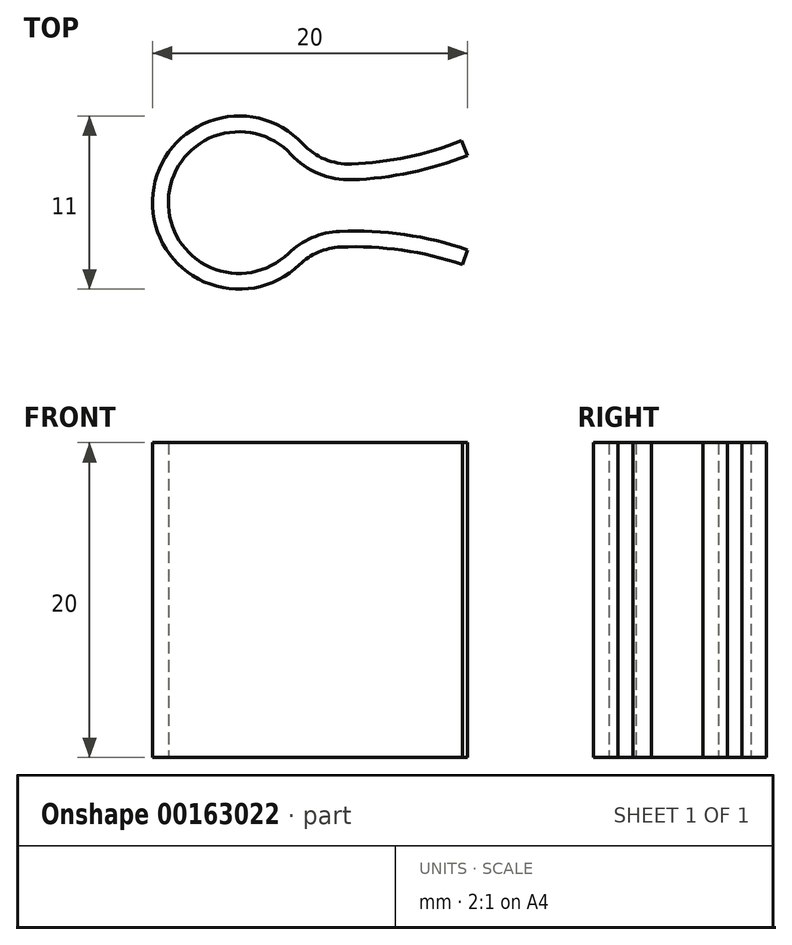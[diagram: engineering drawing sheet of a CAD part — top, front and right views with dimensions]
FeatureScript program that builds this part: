
annotation { "Feature Type Name" : "Feature", "Feature Type Description" : "" }
export const myFeature = defineFeature(function(context is Context, id is Id, definition is map)
    precondition{}
    {
        {
            var Q0;
            Q0=qCreatedBy(makeId("Top.planeOp"),FACE);
            var sketch = newSketch(context, id + "F0", { "sketchPlane" : qUnion([Q0])});
            skArc(sketch, "E0", {"start": v(3.3, 3.05) * mm, "mid": v(-4.5, 0.12) * mm, "end": v(3.13, -3.23) * mm});
            skLineSegment(sketch, "E1", {"start": v(4.5, 0) * mm, "end": v(14.5, 0) * mm});
            skArc(sketch, "E2", {"start": v(7.16, 1.45) * mm, "mid": v(10.9, 1.91) * mm, "end": v(14.5, 3) * mm});
            skPoint(sketch, "E3.visualSharp", {"position": v(4.23, 1.54) * mm});
            skArc(sketch, "E3.filletArc", {"start": v(3.3, 3.05) * mm, "mid": v(5.06, 1.83) * mm, "end": v(7.16, 1.45) * mm});
            skLineSegment(sketch, "E4", {"start": v(0, 0) * mm, "end": v(4.23, 1.54) * mm});
            skArc(sketch, "E5", {"start": v(14.5, -3) * mm, "mid": v(10.5, -2.03) * mm, "end": v(6.39, -1.83) * mm});
            skPoint(sketch, "E6.visualSharp", {"position": v(4, -2.07) * mm});
            skArc(sketch, "E6.filletArc", {"start": v(6.39, -1.83) * mm, "mid": v(4.63, -2.23) * mm, "end": v(3.13, -3.23) * mm});
            skArc(sketch, "E7.0", {"start": v(14.18, -3.95) * mm, "mid": v(10.36, -3.02) * mm, "end": v(6.43, -2.83) * mm});
            skArc(sketch, "E7.1", {"start": v(7.12, 2.45) * mm, "mid": v(10.7, 2.89) * mm, "end": v(14.13, 3.93) * mm});
            skArc(sketch, "E7.2", {"start": v(4.04, 3.73) * mm, "mid": v(5.44, 2.75) * mm, "end": v(7.12, 2.45) * mm});
            skArc(sketch, "E7.3", {"start": v(4.04, 3.73) * mm, "mid": v(-5.5, 0.15) * mm, "end": v(3.83, -3.95) * mm});
            skArc(sketch, "E7.4", {"start": v(6.43, -2.83) * mm, "mid": v(5.03, -3.15) * mm, "end": v(3.83, -3.95) * mm});
            skLineSegment(sketch, "E8", {"start": v(14.13, 3.93) * mm, "end": v(14.5, 3) * mm});
            skLineSegment(sketch, "E9", {"start": v(14.5, -3) * mm, "end": v(14.18, -3.95) * mm});
            skSolve(sketch);
        }
        {
            var Q0;
            Q0=makeQuery(id+"F0.imprint","IMPRINT",FACE,{"disambiguationData":[TD([[makeQuery(id+"F0.imprint","IMPRINT",EDGE,{"derivedFrom":sQuery(id+"F0.wireOp",EDGE,"E0")}),-1.0]])]});
            extrude(context, id + "F1", {"entities" : qUnion([Q0]), "depth" : 20 * mm});
        }
    });
